annotation { "Feature Type Name" : "Feature", "Feature Type Description" : "" }
export const myFeature = defineFeature(function(context is Context, id is Id, definition is map)
    precondition{}
    {
        {
            var Q0;
            Q0=qCreatedBy(makeId("Top.planeOp"),FACE);
            var sketch = newSketch(context, id + "F0", { "sketchPlane" : qUnion([Q0])});
            skLineSegment(sketch, "E0.bottom", {"start": v(-23.87, 30) * mm, "end": v(56.13, 30) * mm});
            skLineSegment(sketch, "E0.top", {"start": v(-23.87, -30) * mm, "end": v(56.13, -30) * mm});
            skLineSegment(sketch, "E0.left", {"start": v(-23.87, 30) * mm, "end": v(-23.87, -30) * mm});
            skLineSegment(sketch, "E0.right", {"start": v(56.13, 30) * mm, "end": v(56.13, -30) * mm});
            skLineSegment(sketch, "E1", {"start": v(-23.87, 30) * mm, "end": v(-49.62, 4.24) * mm});
            skLineSegment(sketch, "E2", {"start": v(-49.62, -4.24) * mm, "end": v(-23.87, -30) * mm});
            skPoint(sketch, "E3.visualSharp", {"position": v(-53.87, 0) * mm});
            skArc(sketch, "E3.filletArc", {"start": v(-49.62, 4.24) * mm, "mid": v(-51.38, 0) * mm, "end": v(-49.62, -4.24) * mm});
            skCircle(sketch, "E4", {"center": v(-45.87, 0) * mm, "radius": 2.5 * mm});
            skSolve(sketch);
        }
        {
            var Q0;
            Q0=makeQuery(id+"F0.imprint","IMPRINT",FACE,{"disambiguationData":[TD([[makeQuery(id+"F0.imprint","IMPRINT",EDGE,{"derivedFrom":sQuery(id+"F0.wireOp",EDGE,"E0.left")}),-1.0]])]});
            var Q1;
            Q1=makeQuery(id+"F0.imprint","IMPRINT",FACE,{"disambiguationData":[TD([[makeQuery(id+"F0.imprint","IMPRINT",EDGE,{"derivedFrom":sQuery(id+"F0.wireOp",EDGE,"E0.bottom")}),-1.0]])]});
            extrude(context, id + "F1", {"entities" : qUnion([Q0, Q1]), "depth" : 2.4 * mm, "offsetDistance" : 25 * mm});
        }
        {
            var Q0;
            Q0=makeQuery(id+"F1.opExtrude","CAP_FACE",FACE,{"disambiguationData":[OSD([sQuery(id+"F0.wireOp",EDGE,"E0.bottom"),sQuery(id+"F0.wireOp",EDGE,"E0.top"),sQuery(id+"F0.wireOp",EDGE,"E0.right"),sQuery(id+"F0.wireOp",EDGE,"E1"),sQuery(id+"F0.wireOp",EDGE,"E2"),sQuery(id+"F0.wireOp",EDGE,"E3.filletArc"),sQuery(id+"F0.wireOp",EDGE,"E4")])],"isStart":false});
            var sketch = newSketch(context, id + "F2", { "sketchPlane" : qUnion([Q0])});
            skText(sketch, "E5", { "text": "Charles Putney\n18 Quinns Road\nShankill, Co. Dublin\nIRELAND", "fontName": "OpenSans-Regular.ttf"});
            const initialGuessF2  = {"E5": [-0.01887, 0.01936, 1, 0, 0.00564]};
            skSetInitialGuess(sketch, initialGuessF2);
            skSolve(sketch);
        }
        {
            var Q0;
            Q0=qSketchRegion(id+"F2",true);
            extrude(context, id + "F3", {"entities" : qUnion([Q0]), "operationType" : NewBodyOperationType.REMOVE, "oppositeDirection" : true, "depth" : 1.2 * mm, "offsetDistance" : 25 * mm});
        }
    });